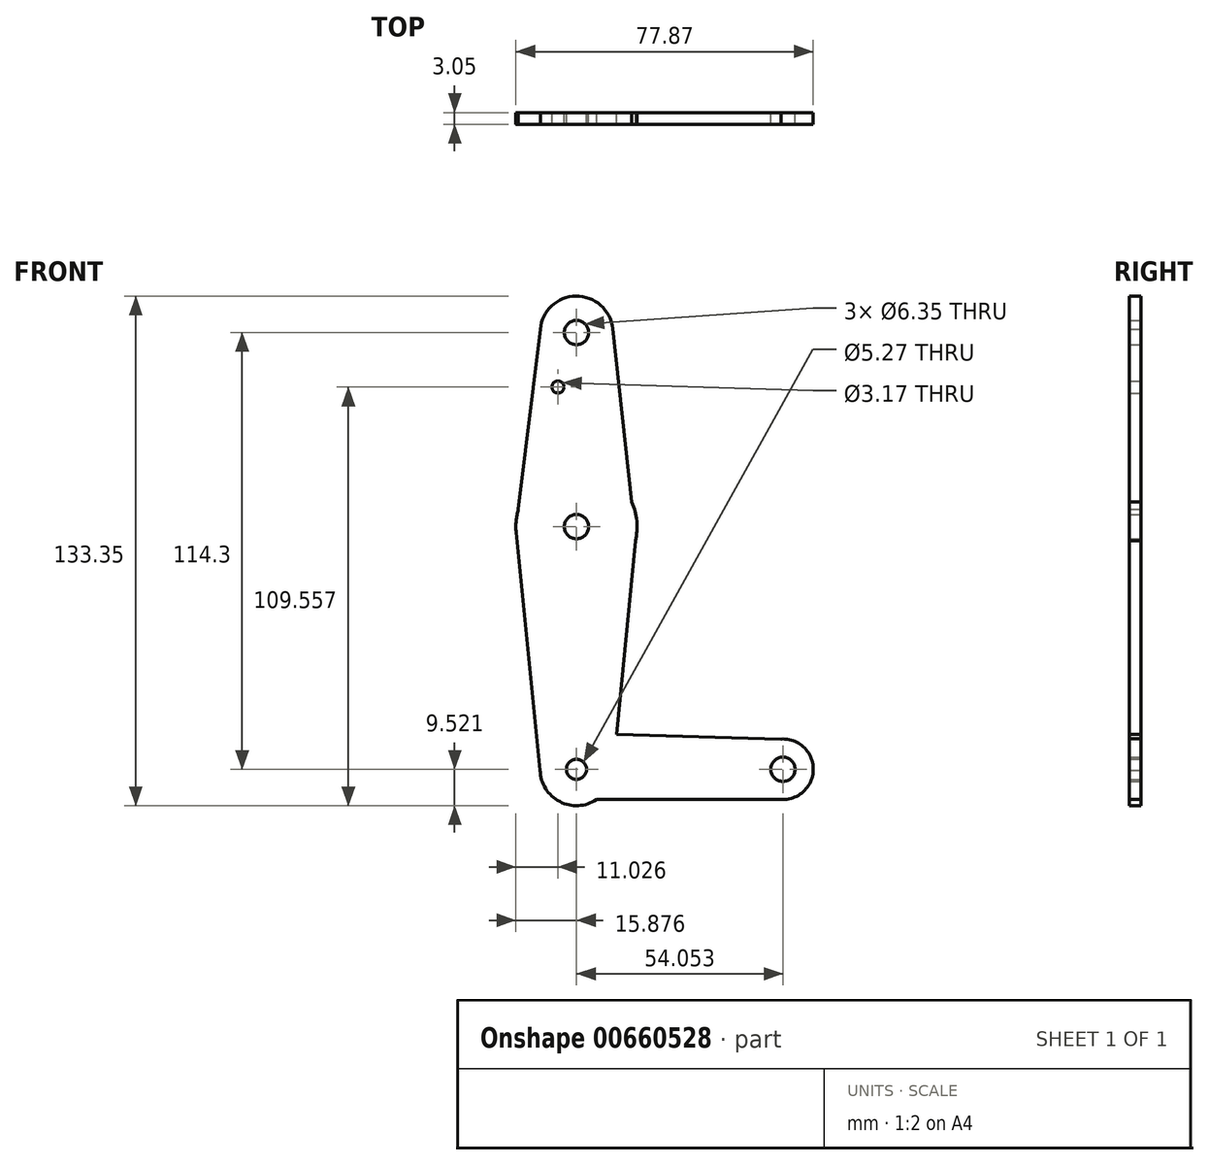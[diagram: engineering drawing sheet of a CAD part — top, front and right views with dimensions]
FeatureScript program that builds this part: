
annotation { "Feature Type Name" : "Feature", "Feature Type Description" : "" }
export const myFeature = defineFeature(function(context is Context, id is Id, definition is map)
    precondition{}
    {
        {
            var Q0;
            Q0=qCreatedBy(makeId("Front.planeOp"),FACE);
            var sketch = newSketch(context, id + "F0", { "sketchPlane" : qUnion([Q0])});
            skLineSegment(sketch, "E0", {"start": v(2.75, 97.33) * mm, "end": v(2.75, 46.53) * mm, "construction": true});
            skLineSegment(sketch, "E1", {"start": v(2.75, 46.53) * mm, "end": v(2.75, -16.97) * mm, "construction": true});
            skLineSegment(sketch, "E2", {"start": v(2.75, -16.97) * mm, "end": v(56.8, -16.97) * mm, "construction": true});
            skCircle(sketch, "E3", {"center": v(56.8, -16.97) * mm, "radius": 7.94 * mm});
            skCircle(sketch, "E4", {"center": v(2.75, -16.97) * mm, "radius": 9.53 * mm});
            skCircle(sketch, "E5", {"center": v(2.75, 46.53) * mm, "radius": 15.88 * mm});
            skCircle(sketch, "E6", {"center": v(2.75, 97.33) * mm, "radius": 9.53 * mm});
            skLineSegment(sketch, "E7", {"start": v(17.25, 52.99) * mm, "end": v(12.21, 98.38) * mm});
            skLineSegment(sketch, "E8", {"start": v(-6.74, 98.15) * mm, "end": v(-12.47, 51.05) * mm});
            skLineSegment(sketch, "E9", {"start": v(18.18, 42.82) * mm, "end": v(12.23, -17.9) * mm});
            skLineSegment(sketch, "E10", {"start": v(-6.78, -17.2) * mm, "end": v(-13.05, 44.94) * mm});
            skLineSegment(sketch, "E11", {"start": v(3.9, -7.51) * mm, "end": v(57.76, -9.09) * mm});
            skLineSegment(sketch, "E12", {"start": v(56.8, -24.9) * mm, "end": v(3.9, -24.9) * mm});
            skCircle(sketch, "E13", {"center": v(-2.1, 83.07) * mm, "radius": 1.59 * mm});
            skCircle(sketch, "E14", {"center": v(2.75, 97.33) * mm, "radius": 3.18 * mm});
            skCircle(sketch, "E15", {"center": v(2.75, 46.53) * mm, "radius": 3.18 * mm});
            skCircle(sketch, "E16", {"center": v(2.75, -16.97) * mm, "radius": 2.63 * mm});
            skCircle(sketch, "E17", {"center": v(56.8, -16.97) * mm, "radius": 3.18 * mm});
            skSolve(sketch);
        }
        {
            var Q0;
            Q0 = qSketchRegion(id + "F0", true);
            extrude(context, id + "F1", {"entities" : qUnion([Q0]), "depth" : 3.05 * mm, "offsetDistance" : 25.4 * mm});
        }
    });
